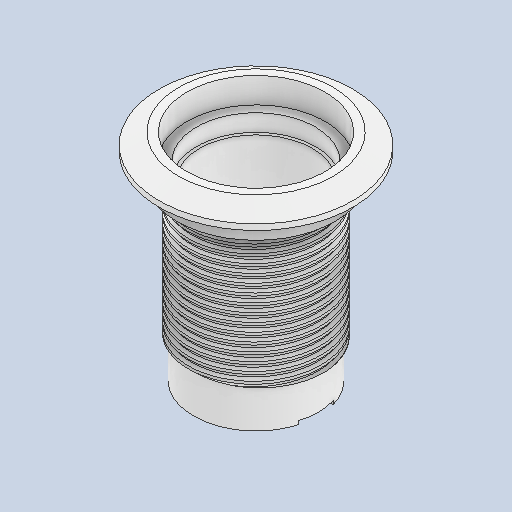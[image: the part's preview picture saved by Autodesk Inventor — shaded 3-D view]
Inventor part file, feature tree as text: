
AUTODESK INVENTOR PART (.ipt)
format: ipt  version: 2022 (Build 260153000, 153)  size: 725,504 bytes
history: native  units: in
note: dims shown in document units (in); Inventor stores cm internally (conversion verified against a paired STEP export)
features: thread x1
ambient origin geometry x8: Origin, YZ Plane, XZ Plane, XY Plane, X Axis, Y Axis, Z Axis, Center Point
bodies: Solid1 (feature_tree)
feature tree (1):
  thread  "Gewinde"  [1 undecoded]
note: 1 required parameter value undecoded (feature->parameter linkage not recoverable at this tier; creation-order binding heuristic only, values carry confidence <= 0.55)
